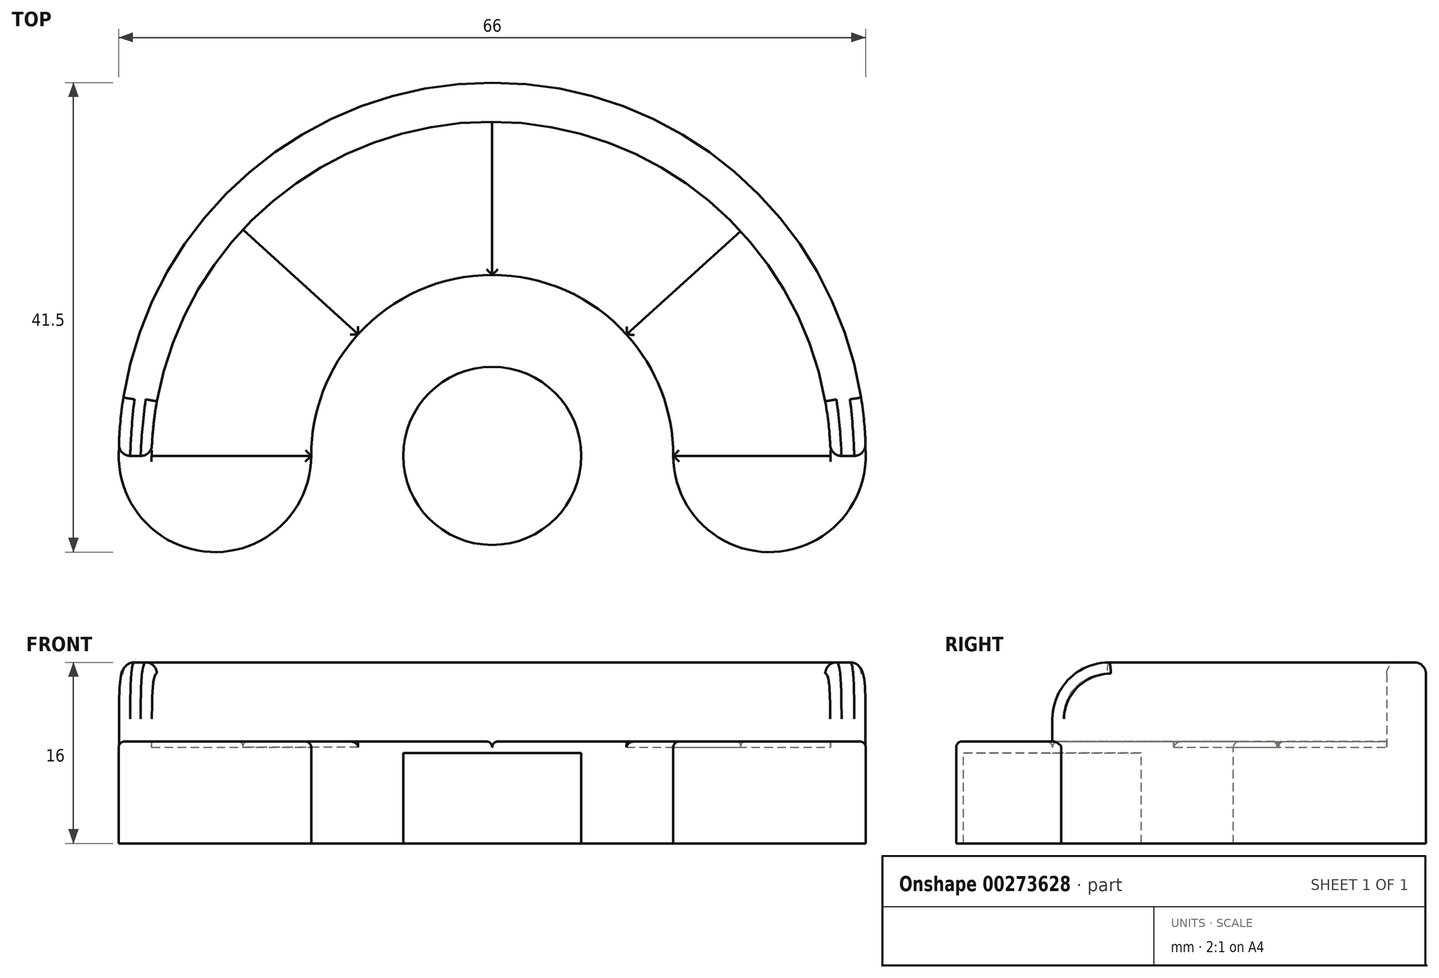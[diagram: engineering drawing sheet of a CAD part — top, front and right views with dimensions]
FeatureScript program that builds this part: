
annotation { "Feature Type Name" : "Feature", "Feature Type Description" : "" }
export const myFeature = defineFeature(function(context is Context, id is Id, definition is map)
    precondition{}
    {
        {
            var Q0;
            Q0=qCreatedBy(makeId("Top.planeOp"),FACE);
            var sketch = newSketch(context, id + "F0", { "sketchPlane" : qUnion([Q0])});
            skArc(sketch, "E0", {"start": v(16, 0) * mm, "mid": v(0, 16) * mm, "end": v(-16, 0) * mm});
            skCircle(sketch, "E1", {"center": v(0, 0) * mm, "radius": 7.87 * mm});
            skArc(sketch, "E2", {"start": v(33, 0) * mm, "mid": v(0, 33) * mm, "end": v(-33, 0) * mm});
            skLineSegment(sketch, "E3", {"start": v(-30.1, 0) * mm, "end": v(-33, 0) * mm});
            skArc(sketch, "E4", {"start": v(-33, 0) * mm, "mid": v(-24.5, -8.5) * mm, "end": v(-16, 0) * mm});
            skArc(sketch, "E5", {"start": v(16, 0) * mm, "mid": v(24.5, -8.5) * mm, "end": v(33, 0) * mm});
            skArc(sketch, "E6.trimOffspring", {"start": v(29.9, 0) * mm, "mid": v(-0.1, 29.53) * mm, "end": v(-30.1, 0) * mm});
            skLineSegment(sketch, "E7.trimOffspring", {"start": v(29.9, 0) * mm, "end": v(33, 0) * mm});
            skPoint(sketch, "E8.start.orphan", {"position": v(16, 0) * mm});
            skPoint(sketch, "E9.endSnap0", {"position": v(-0.1, 29.53) * mm});
            skLineSegment(sketch, "E10", {"start": v(-11.84, 10.76) * mm, "end": v(-22.03, 20) * mm});
            skLineSegment(sketch, "E11", {"start": v(0, 16) * mm, "end": v(0, 29.53) * mm});
            skLineSegment(sketch, "E12", {"start": v(11.87, 10.73) * mm, "end": v(21.96, 19.86) * mm});
            skLineSegment(sketch, "E13", {"start": v(-30.1, 0) * mm, "end": v(-16, 0) * mm});
            skLineSegment(sketch, "E14", {"start": v(16, 0) * mm, "end": v(29.9, 0) * mm});
            skSolve(sketch);
        }
        {
            var Q0;
            Q0=makeQuery(id+"F0.imprint","IMPRINT",FACE,{"disambiguationData":[TD([[makeQuery(id+"F0.imprint","IMPRINT",EDGE,{"derivedFrom":sQuery(id+"F0.wireOp",EDGE,"E2")}),1.0]])]});
            var Q1;
            {var subQ0=sQuery(id+"F0.wireOp",EDGE,"E10");Q1=makeQuery(id+"F0.imprint","IMPRINT",FACE,{"disambiguationData":[TD([[makeQuery(id+"F0.imprint","IMPRINT",EDGE,{"derivedFrom":subQ0}),-1.0]])]});}
            var Q2;
            {var subQ2=sQuery(id+"F0.wireOp",EDGE,"E10");Q2=makeQuery(id+"F0.imprint","IMPRINT",FACE,{"disambiguationData":[TD([[makeQuery(id+"F0.imprint","IMPRINT",EDGE,{"derivedFrom":subQ2}),1.0]])]});}
            var Q3;
            {var subQ0=sQuery(id+"F0.wireOp",EDGE,"E11");Q3=makeQuery(id+"F0.imprint","IMPRINT",FACE,{"disambiguationData":[TD([[makeQuery(id+"F0.imprint","IMPRINT",EDGE,{"derivedFrom":subQ0}),-1.0]])]});}
            var Q4;
            {var subQ2=sQuery(id+"F0.wireOp",EDGE,"E12");Q4=makeQuery(id+"F0.imprint","IMPRINT",FACE,{"disambiguationData":[TD([[makeQuery(id+"F0.imprint","IMPRINT",EDGE,{"derivedFrom":subQ2}),-1.0]])]});}
            var Q5;
            Q5=makeQuery(id+"F0.imprint","IMPRINT",FACE,{"disambiguationData":[TD([[makeQuery(id+"F0.imprint","IMPRINT",EDGE,{"derivedFrom":sQuery(id+"F0.wireOp",EDGE,"E5")}),1.0]])]});
            var Q6;
            Q6=makeQuery(id+"F0.imprint","IMPRINT",FACE,{"disambiguationData":[TD([[makeQuery(id+"F0.imprint","IMPRINT",EDGE,{"derivedFrom":sQuery(id+"F0.wireOp",EDGE,"E3")}),1.0]])]});
            var Q7;
            Q7=makeQuery(id+"F0.imprint","IMPRINT",FACE,{"disambiguationData":[TD([[makeQuery(id+"F0.imprint","IMPRINT",EDGE,{"derivedFrom":sQuery(id+"F0.wireOp",EDGE,"E1")}),1.0]])]});
            extrude(context, id + "F1", {"entities" : qUnion([Q0, Q1, Q2, Q3, Q4, Q5, Q6, Q7]), "oppositeDirection" : true, "depth" : 8 * mm});
        }
        {
            var Q0;
            Q0=makeQuery(id+"F0.imprint","IMPRINT",FACE,{"disambiguationData":[TD([[makeQuery(id+"F0.imprint","IMPRINT",EDGE,{"derivedFrom":sQuery(id+"F0.wireOp",EDGE,"E2")}),1.0]])]});
            extrude(context, id + "F2", {"entities" : qUnion([Q0]), "operationType" : NewBodyOperationType.ADD, "depth" : 8 * mm});
        }
        {
            var Q0;
            Q0=makeQuery(id+"F0.imprint","IMPRINT",FACE,{"disambiguationData":[TD([[makeQuery(id+"F0.imprint","IMPRINT",EDGE,{"derivedFrom":sQuery(id+"F0.wireOp",EDGE,"E3")}),1.0]])]});
            var Q1;
            {var subQ0=sQuery(id+"F0.wireOp",EDGE,"E10");Q1=makeQuery(id+"F0.imprint","IMPRINT",FACE,{"disambiguationData":[TD([[makeQuery(id+"F0.imprint","IMPRINT",EDGE,{"derivedFrom":subQ0}),-1.0]])]});}
            var Q2;
            {var subQ2=sQuery(id+"F0.wireOp",EDGE,"E12");Q2=makeQuery(id+"F0.imprint","IMPRINT",FACE,{"disambiguationData":[TD([[makeQuery(id+"F0.imprint","IMPRINT",EDGE,{"derivedFrom":subQ2}),-1.0]])]});}
            extrude(context, id + "F3", {"entities" : qUnion([Q0, Q1, Q2]), "operationType" : NewBodyOperationType.ADD, "depth" : 1 * mm});
        }
        {
            var Q0;
            {var subQ0=sQuery(id+"F0.wireOp",EDGE,"E13");var subQ1=sQuery(id+"F0.wireOp",EDGE,"E4");var subQ2=sQuery(id+"F0.wireOp",EDGE,"E3");Q0=makeQuery(id+"F3.boolean.opBoolean","SPLIT",EDGE,{"disambiguationData":[TD([makeQuery(id+"F1.opExtrude","SWEPT_FACE",FACE,{"disambiguationData":[OSD([subQ1])]}),makeQuery(id+"F2.opExtrude","SWEPT_FACE",FACE,{"disambiguationData":[OSD([subQ2])]}),makeQuery(id+"F2.opExtrude","SWEPT_FACE",FACE,{"disambiguationData":[OSD([sQuery(id+"F0.wireOp",EDGE,"E6.trimOffspring")])]}),makeQuery(id+"F3.opExtrude","CAP_FACE",FACE,{"disambiguationData":[OSD([subQ2,subQ1,subQ0])],"isStart":false}),makeQuery(id+"F3.opExtrude","SWEPT_FACE",FACE,{"disambiguationData":[OSD([subQ2,subQ0])]}),makeQuery(id+"F3.opExtrude","SWEPT_FACE",FACE,{"disambiguationData":[OSD([subQ1])]})])],"derivedFrom":makeQuery(id+"F3.opExtrude","CAP_EDGE",EDGE,{"disambiguationData":[OSD([subQ2,subQ0])],"isStart":false})});}
            var Q1;
            Q1=makeQuery(id+"F3.opExtrude","CAP_EDGE",EDGE,{"disambiguationData":[OSD([sQuery(id+"F0.wireOp",EDGE,"E4")])],"isStart":false});
            var Q2;
            Q2=makeQuery(id+"F3.opExtrude","CAP_EDGE",EDGE,{"disambiguationData":[OSD([sQuery(id+"F0.wireOp",EDGE,"E10")])],"isStart":false});
            var Q3;
            {var subQ0=sQuery(id+"F0.wireOp",EDGE,"E0");Q3=makeQuery(id+"F3.opExtrude","CAP_EDGE",EDGE,{"disambiguationData":[OSD([subQ0]),TDD([makeQuery(id+"F0.imprint","IMPRINT",EDGE,{"disambiguationData":[TD([[makeQuery(id+"F0.imprint","INTERSECT",VERTEX,{"derivedFrom":[subQ0,sQuery(id+"F0.wireOp",EDGE,"E10")]}),1.0]])],"derivedFrom":subQ0})])],"isStart":false});}
            var Q4;
            Q4=makeQuery(id+"F3.opExtrude","CAP_EDGE",EDGE,{"disambiguationData":[OSD([sQuery(id+"F0.wireOp",EDGE,"E11")])],"isStart":false});
            var Q5;
            Q5=makeQuery(id+"F3.opExtrude","CAP_EDGE",EDGE,{"disambiguationData":[OSD([sQuery(id+"F0.wireOp",EDGE,"E12")])],"isStart":false});
            var Q6;
            Q6=makeQuery(id+"F3.opExtrude","CAP_EDGE",EDGE,{"disambiguationData":[OSD([sQuery(id+"F0.wireOp",EDGE,"E14")])],"isStart":false});
            var Q7;
            {var subQ0=sQuery(id+"F0.wireOp",EDGE,"E0");Q7=makeQuery(id+"F3.opExtrude","CAP_EDGE",EDGE,{"disambiguationData":[OSD([subQ0]),TDD([makeQuery(id+"F0.imprint","IMPRINT",EDGE,{"disambiguationData":[TD([[makeQuery(id+"F0.imprint","INTERSECT",VERTEX,{"derivedFrom":[subQ0,sQuery(id+"F0.wireOp",EDGE,"E12")]}),1.0]])],"derivedFrom":subQ0})])],"isStart":false});}
            fillet(context, id + "F4", {"entities" : qUnion([Q0, Q1, Q2, Q3, Q4, Q5, Q6, Q7]), "radius" : 0.5 * mm, "tangentPropagation" : true, "allowEdgeOverflow" : false});
        }
        {
            var Q0;
            {var subQ2=sQuery(id+"F0.wireOp",EDGE,"E10");Q0=makeQuery(id+"F0.imprint","IMPRINT",FACE,{"disambiguationData":[TD([[makeQuery(id+"F0.imprint","IMPRINT",EDGE,{"derivedFrom":subQ2}),1.0]])]});}
            var Q1;
            {var subQ0=sQuery(id+"F0.wireOp",EDGE,"E11");Q1=makeQuery(id+"F0.imprint","IMPRINT",FACE,{"disambiguationData":[TD([[makeQuery(id+"F0.imprint","IMPRINT",EDGE,{"derivedFrom":subQ0}),-1.0]])]});}
            var Q2;
            Q2=makeQuery(id+"F0.imprint","IMPRINT",FACE,{"disambiguationData":[TD([[makeQuery(id+"F0.imprint","IMPRINT",EDGE,{"derivedFrom":sQuery(id+"F0.wireOp",EDGE,"E5")}),1.0]])]});
            extrude(context, id + "F5", {"entities" : qUnion([Q0, Q1, Q2]), "operationType" : NewBodyOperationType.ADD, "depth" : 1 * mm});
        }
        {
            var Q0;
            Q0=makeQuery(id+"F5.opExtrude","CAP_EDGE",EDGE,{"disambiguationData":[OSD([sQuery(id+"F0.wireOp",EDGE,"E13")])],"isStart":false});
            var Q1;
            {var subQ0=sQuery(id+"F0.wireOp",EDGE,"E0");Q1=makeQuery(id+"F5.opExtrude","CAP_EDGE",EDGE,{"disambiguationData":[OSD([subQ0]),TDD([makeQuery(id+"F0.imprint","IMPRINT",EDGE,{"disambiguationData":[TD([[makeQuery(id+"F0.imprint","INTERSECT",VERTEX,{"derivedFrom":[subQ0,sQuery(id+"F0.wireOp",EDGE,"E10")]}),-1.0]])],"derivedFrom":subQ0})])],"isStart":false});}
            var Q2;
            Q2=makeQuery(id+"F5.opExtrude","CAP_EDGE",EDGE,{"disambiguationData":[OSD([sQuery(id+"F0.wireOp",EDGE,"E10")])],"isStart":false});
            var Q3;
            Q3=makeQuery(id+"F5.opExtrude","CAP_EDGE",EDGE,{"disambiguationData":[OSD([sQuery(id+"F0.wireOp",EDGE,"E11")])],"isStart":false});
            var Q4;
            {var subQ0=sQuery(id+"F0.wireOp",EDGE,"E0");Q4=makeQuery(id+"F5.opExtrude","CAP_EDGE",EDGE,{"disambiguationData":[OSD([subQ0]),TDD([makeQuery(id+"F0.imprint","IMPRINT",EDGE,{"disambiguationData":[TD([[makeQuery(id+"F0.imprint","INTERSECT",VERTEX,{"derivedFrom":[subQ0,sQuery(id+"F0.wireOp",EDGE,"E11")]}),1.0]])],"derivedFrom":subQ0})])],"isStart":false});}
            var Q5;
            Q5=makeQuery(id+"F5.opExtrude","CAP_EDGE",EDGE,{"disambiguationData":[OSD([sQuery(id+"F0.wireOp",EDGE,"E12")])],"isStart":false});
            var Q6;
            Q6=makeQuery(id+"F5.opExtrude","CAP_EDGE",EDGE,{"disambiguationData":[OSD([sQuery(id+"F0.wireOp",EDGE,"E14")])],"isStart":false});
            var Q7;
            Q7=makeQuery(id+"F5.opExtrude","CAP_EDGE",EDGE,{"disambiguationData":[OSD([sQuery(id+"F0.wireOp",EDGE,"E5")])],"isStart":false});
            fillet(context, id + "F6", {"entities" : qUnion([Q0, Q1, Q2, Q3, Q4, Q5, Q6, Q7]), "radius" : 0.5 * mm, "tangentPropagation" : true, "allowEdgeOverflow" : false});
        }
        {
            var Q0;
            Q0=makeQuery(id+"F2.opExtrude","CAP_EDGE",EDGE,{"disambiguationData":[OSD([sQuery(id+"F0.wireOp",EDGE,"E3")])],"isStart":false});
            var Q1;
            Q1=makeQuery(id+"F2.opExtrude","CAP_EDGE",EDGE,{"disambiguationData":[OSD([sQuery(id+"F0.wireOp",EDGE,"E7.trimOffspring")])],"isStart":false});
            fillet(context, id + "F7", {"entities" : qUnion([Q0, Q1]), "radius" : 5 * mm, "tangentPropagation" : true, "allowEdgeOverflow" : false});
        }
        {
            var Q0;
            Q0=makeQuery(id+"F2.opExtrude","CAP_EDGE",EDGE,{"disambiguationData":[OSD([sQuery(id+"F0.wireOp",EDGE,"E2")])],"isStart":false});
            var Q1;
            Q1=makeQuery(id+"F2.opExtrude","CAP_EDGE",EDGE,{"disambiguationData":[OSD([sQuery(id+"F0.wireOp",EDGE,"E6.trimOffspring")])],"isStart":false});
            fillet(context, id + "F8", {"entities" : qUnion([Q0, Q1]), "radius" : 1 * mm, "tangentPropagation" : true, "allowEdgeOverflow" : false});
        }
    });
